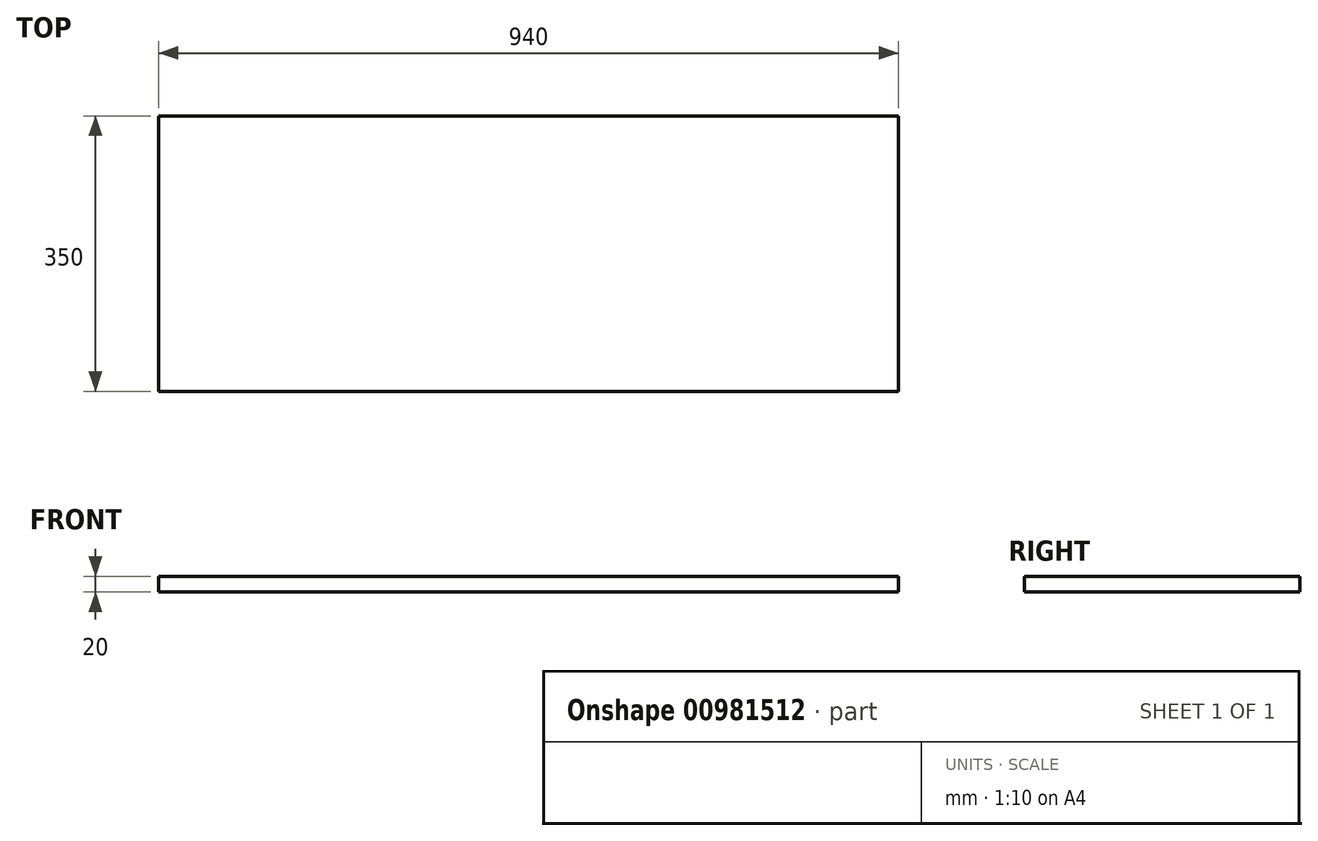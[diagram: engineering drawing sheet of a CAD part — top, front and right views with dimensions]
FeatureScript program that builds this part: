
annotation { "Feature Type Name" : "Feature", "Feature Type Description" : "" }
export const myFeature = defineFeature(function(context is Context, id is Id, definition is map)
    precondition{}
    {
        {
            var Q0;
            Q0=qCreatedBy(makeId("Top.planeOp"),FACE);
            var sketch = newSketch(context, id + "F0", { "sketchPlane" : qUnion([Q0])});
            skLineSegment(sketch, "E0.bottom", {"start": v(-477.26, 48.85) * mm, "end": v(462.74, 48.85) * mm});
            skLineSegment(sketch, "E0.top", {"start": v(-477.26, -301.15) * mm, "end": v(462.74, -301.15) * mm});
            skLineSegment(sketch, "E0.left", {"start": v(-477.26, 48.85) * mm, "end": v(-477.26, -301.15) * mm});
            skLineSegment(sketch, "E0.right", {"start": v(462.74, 48.85) * mm, "end": v(462.74, -301.15) * mm});
            skSolve(sketch);
        }
        {
            var Q0;
            Q0=makeQuery(id+"F0.imprint","IMPRINT",FACE,{"disambiguationData":[TD([[makeQuery(id+"F0.imprint","IMPRINT",EDGE,{"derivedFrom":sQuery(id+"F0.wireOp",EDGE,"E0.bottom")}),-1.0]])]});
            extrude(context, id + "F1", {"entities" : qUnion([Q0]), "depth" : 20 * mm, "offsetDistance" : 25 * mm});
        }
    });
